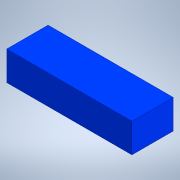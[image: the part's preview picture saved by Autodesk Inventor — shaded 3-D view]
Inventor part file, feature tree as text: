
AUTODESK INVENTOR PART (.ipt)
format: ipt  version: 2020.4 (Build 244396000, 396)  size: 96,256 bytes
history: native  units: mm
features: extrude x1, sketch x1
ambient origin geometry x8: Origin, YZ Plane, XZ Plane, XY Plane, X Axis, Y Axis, Z Axis, Center Point
bodies: Solid1 (feature_tree)
feature tree (2):
  extrude  "Extrusion1"  Depth=34.0mm
  sketch  "Sketch1"  dims[d0=103.0mm d1=34.0mm d2=24.0mm d3=0.0mm]
